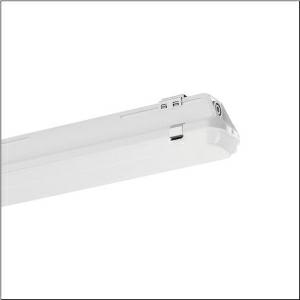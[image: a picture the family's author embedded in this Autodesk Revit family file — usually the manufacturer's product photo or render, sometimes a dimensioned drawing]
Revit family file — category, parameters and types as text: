
# Revit family: monsun_r__11_parking_51fg207p440h_0f51
name_source: partatom
category: Lighting Fixtures
units: mm (PartAtom-declared; Revit-internal decimal feet)

## family parameters
Cut with Voids When Loaded = No
Host = Face
Light Source = No
Part Type = Normal
Room Calculation Point = No
Round Connector Dimension = Use Diameter
Shared = No

## types (1)
- Monsun® 11 parking (1 x LED, 4820 lm, 29.2 W, 4000K)
    Apparent Load = 29 VA
    CIE Flux Codes = 45 75 93 94 100
    Color Rendering = 80
    Color Temperature = 4000K
    Default Elevation = 1800 mm
    Description = Monsun® 11 parking, damp-proof luminaire, chain hanger, primary optical cover: enclosure, of PC, light emission: direct distribution, primary light characteristic: symmetric, installation type: suspended mounting, surface-mounted, horizontal mounting, vertical mounting, LED, rated luminous flux: 4.820lm, luminous efficacy: 165lm/W, light colour: 840, colour temperature: 4000K, control gear: ON/OFF, with terminal, 3-pole, max. 2.5mm², mains connection: 220..240V, AC, 50/60Hz, rated input power: 29W, housing, of glass-fibre reinforced polyester, uncoated, bright grey, incl. chain hanger, length: 1.590mm, width: 90mm, height: 88mm, clip for enclosure, of stainless steel (V2A), ceiling mounting element, of stainless steel (V2A), chain hanger, of stainless steel (V2A), protection rating (complete): IP66, insulation class (complete): insulation class I (protective earthing), certification: CE, ENEC, VDE, UKCA, protection symbol: D, impact resistance: IK08, permissible operating ambient temperature: -35..+40°C, standard: EN 50419, EN 60598-2-1, no direct snow, no direct sun, no direct rain, for indoor or canopied outdoor use, corresponds to IFS (International Featured Standards) requirements for safety and quality in the food industry, contact your sales advisor before using the luminaires in applications with unclear chemical exposure, large temperature fluctuations or condensation-forming humidity, LABS conformity tested according to VDMA 24364:2018-05, packaging unit: 1 piece
    Height = 89 mm
    Lamp = 1 x LED
    Lamp Light Flux = 4820 lm
    Lamp Power = 29.2 W
    Lamp count = 1
    Length = 1590 mm
    Luminous efficacy = 165 lm/W
    Manufacturer = Siteco
    ModVariant = No
    Model = 51FG207P440H
    Mounting Place = Ceiling
    Mounting Type = Surface mounted
    Number of Poles = 1
    OnlyDefault = Yes
    Power Factor = 1
    Product Name = Monsun® 11 parking
    Product group = damp-proof luminaire
    ProductGroupID = 301
    Protection Class = Protection class I
    Protection Degree = IP 66
    RLX_Detail_Level = 1
    RLX_Emergency_Light_Flux = 0 lm
    RLX_Emergency_Type = 0
    RLX_Emergency_Type_DB = No
    RlxData = <blob elided: 88389 chars, md5=bc07df4d>
    Socket = socket
    Standby Power = 0 W
    System Light Flux = 4820 lm
    System Power = 29 W
    Type Comments = Product without accessories
    Type Image = l_1349237.jpg
    URL = http://relux.com
    VarID = ---
    Voltage = 0 V
    Weight = 0.00 kg
    Width = 90 mm

## geometry (parser evidence)
native form markers: Blend x4, Sweep x12
no freeform markers — native parametric forms only
